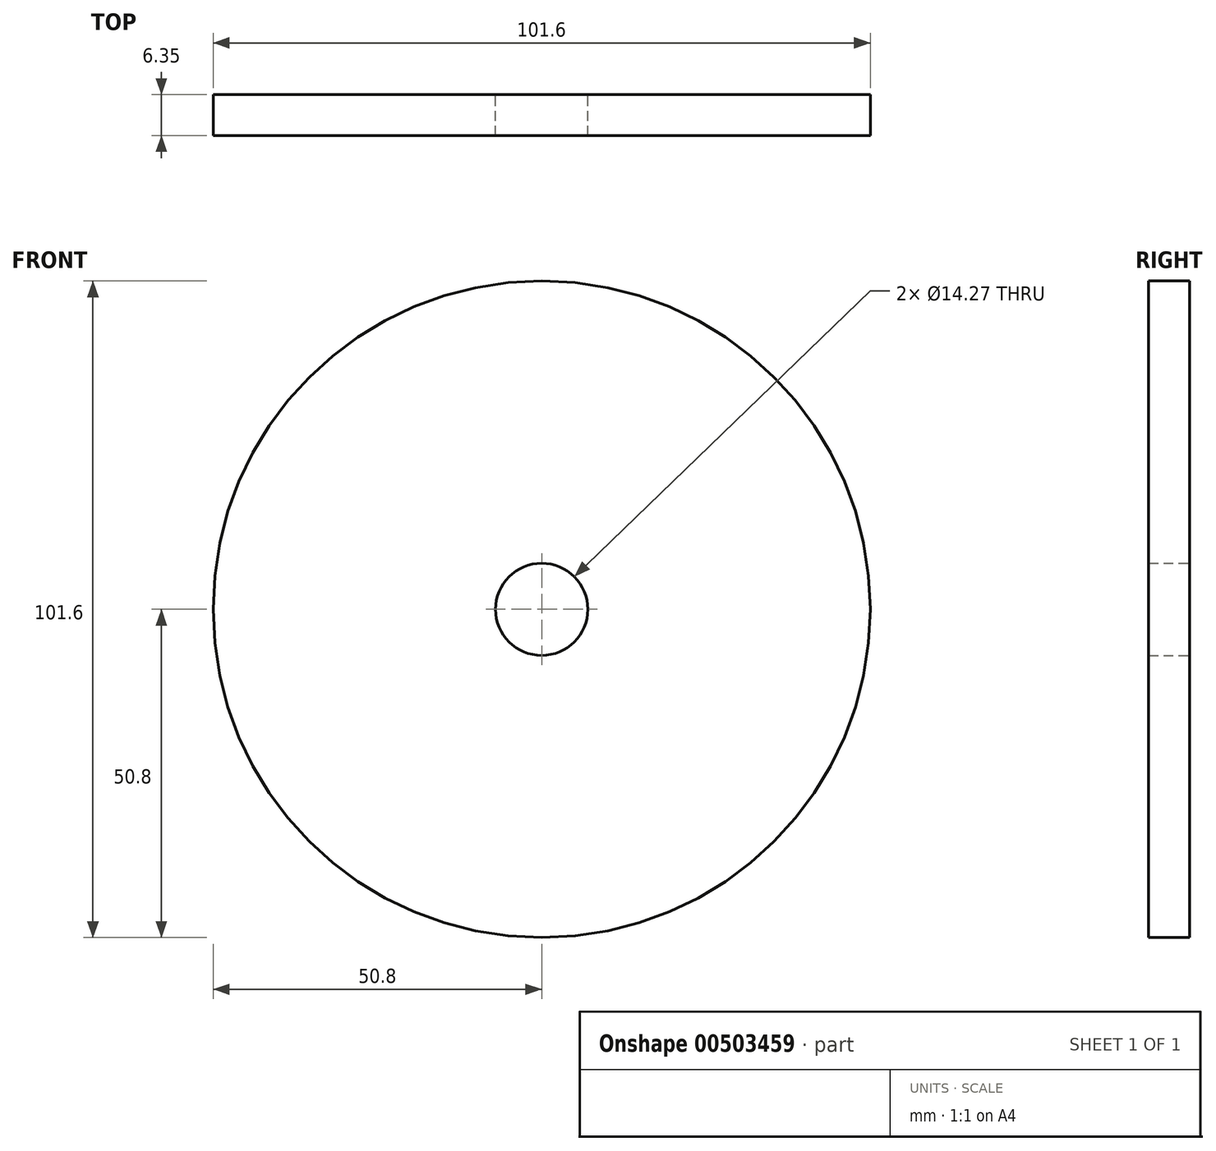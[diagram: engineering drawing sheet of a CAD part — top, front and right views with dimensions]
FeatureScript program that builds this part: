
annotation { "Feature Type Name" : "Feature", "Feature Type Description" : "" }
export const myFeature = defineFeature(function(context is Context, id is Id, definition is map)
    precondition{}
    {
        {
            var Q0;
            Q0=qCreatedBy(makeId("Front.planeOp"),FACE);
            var sketch = newSketch(context, id + "F0", { "sketchPlane" : qUnion([Q0])});
            skCircle(sketch, "E0", {"center": v(0, 0) * mm, "radius": 50.8 * mm});
            skCircle(sketch, "E1", {"center": v(0, 0) * mm, "radius": 7.14 * mm});
            skSolve(sketch);
        }
        {
            var Q0;
            Q0=makeQuery(id+"F0.imprint","IMPRINT",FACE,{"disambiguationData":[TD([[makeQuery(id+"F0.imprint","IMPRINT",EDGE,{"derivedFrom":sQuery(id+"F0.wireOp",EDGE,"E0")}),1.0]])]});
            extrude(context, id + "F1", {"entities" : qUnion([Q0]), "depth" : 6.35 * mm, "offsetDistance" : 25.4 * mm});
        }
    });
